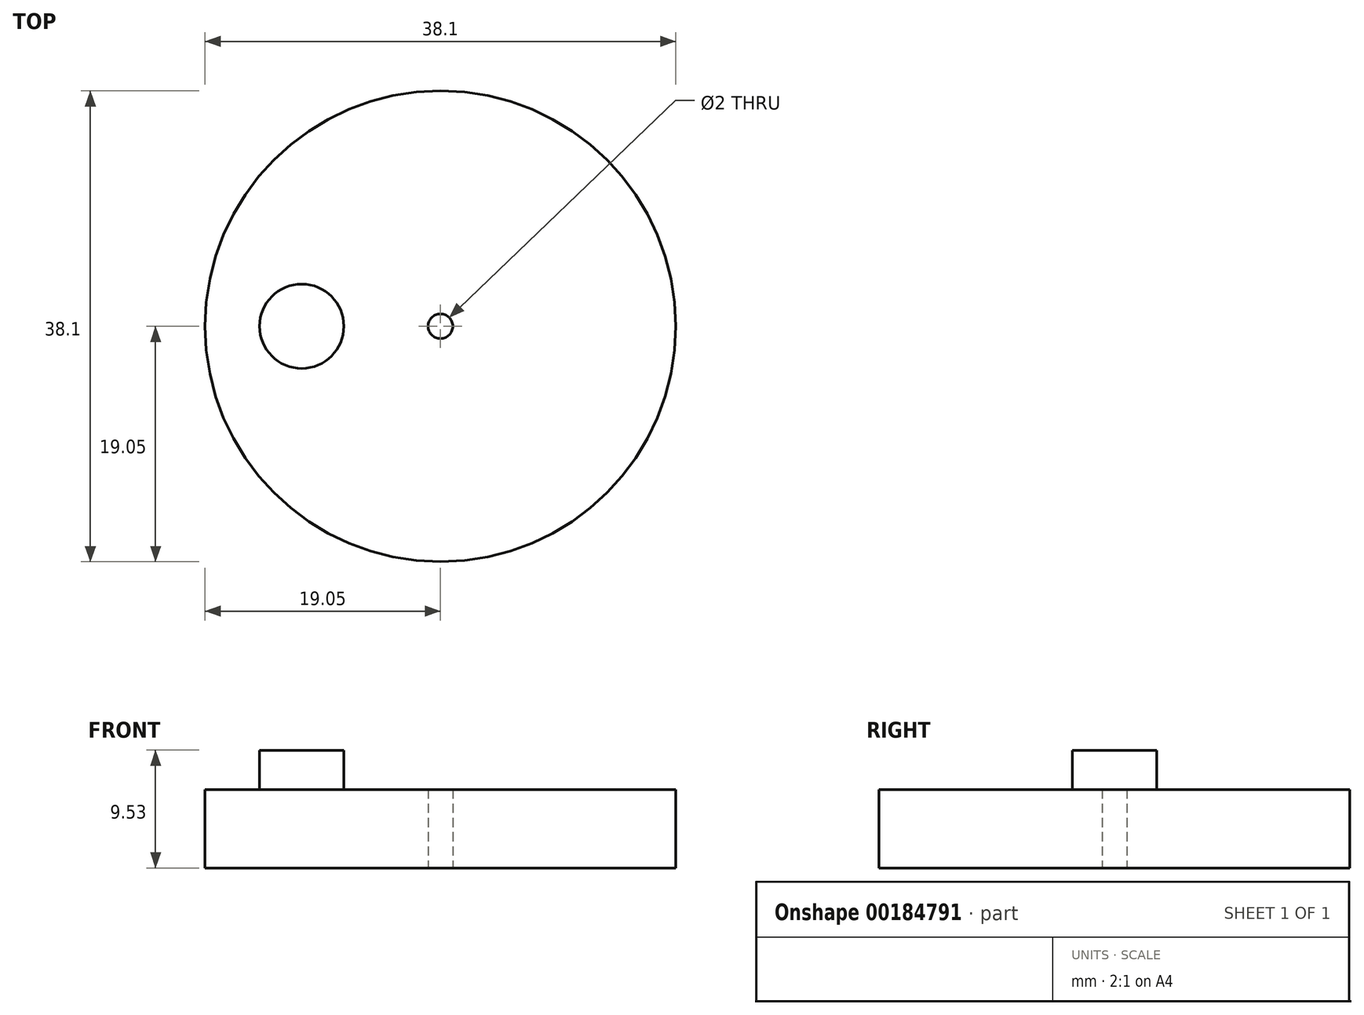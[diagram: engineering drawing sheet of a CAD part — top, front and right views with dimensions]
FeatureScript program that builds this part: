
annotation { "Feature Type Name" : "Feature", "Feature Type Description" : "" }
export const myFeature = defineFeature(function(context is Context, id is Id, definition is map)
    precondition{}
    {
        {
            var Q0;
            Q0=qCreatedBy(makeId("Top.planeOp"),FACE);
            var sketch = newSketch(context, id + "F0", { "sketchPlane" : qUnion([Q0])});
            skCircle(sketch, "E0", {"center": v(0, 0) * mm, "radius": 19.05 * mm});
            skCircle(sketch, "E1", {"center": v(0, 0) * mm, "radius": 1 * mm});
            skSolve(sketch);
        }
        {
            var Q0;
            Q0=makeQuery(id+"F0.imprint","IMPRINT",FACE,{"disambiguationData":[TD([[makeQuery(id+"F0.imprint","IMPRINT",EDGE,{"derivedFrom":sQuery(id+"F0.wireOp",EDGE,"E0")}),1.0]])]});
            extrude(context, id + "F1", {"entities" : qUnion([Q0]), "depth" : 6.35 * mm});
        }
        {
            var Q0;
            Q0=makeQuery(id+"F1.opExtrude","CAP_FACE",FACE,{"disambiguationData":[OSD([sQuery(id+"F0.wireOp",EDGE,"E0"),sQuery(id+"F0.wireOp",EDGE,"E1")])],"isStart":false});
            var sketch = newSketch(context, id + "F2", { "sketchPlane" : qUnion([Q0])});
            skCircle(sketch, "E2", {"center": v(-11.23, 0) * mm, "radius": 3.41 * mm});
            skSolve(sketch);
        }
        {
            var Q0;
            Q0=qSketchRegion(id+"F2",true);
            extrude(context, id + "F3", {"entities" : qUnion([Q0]), "operationType" : NewBodyOperationType.ADD, "depth" : 3.17 * mm});
        }
    });
